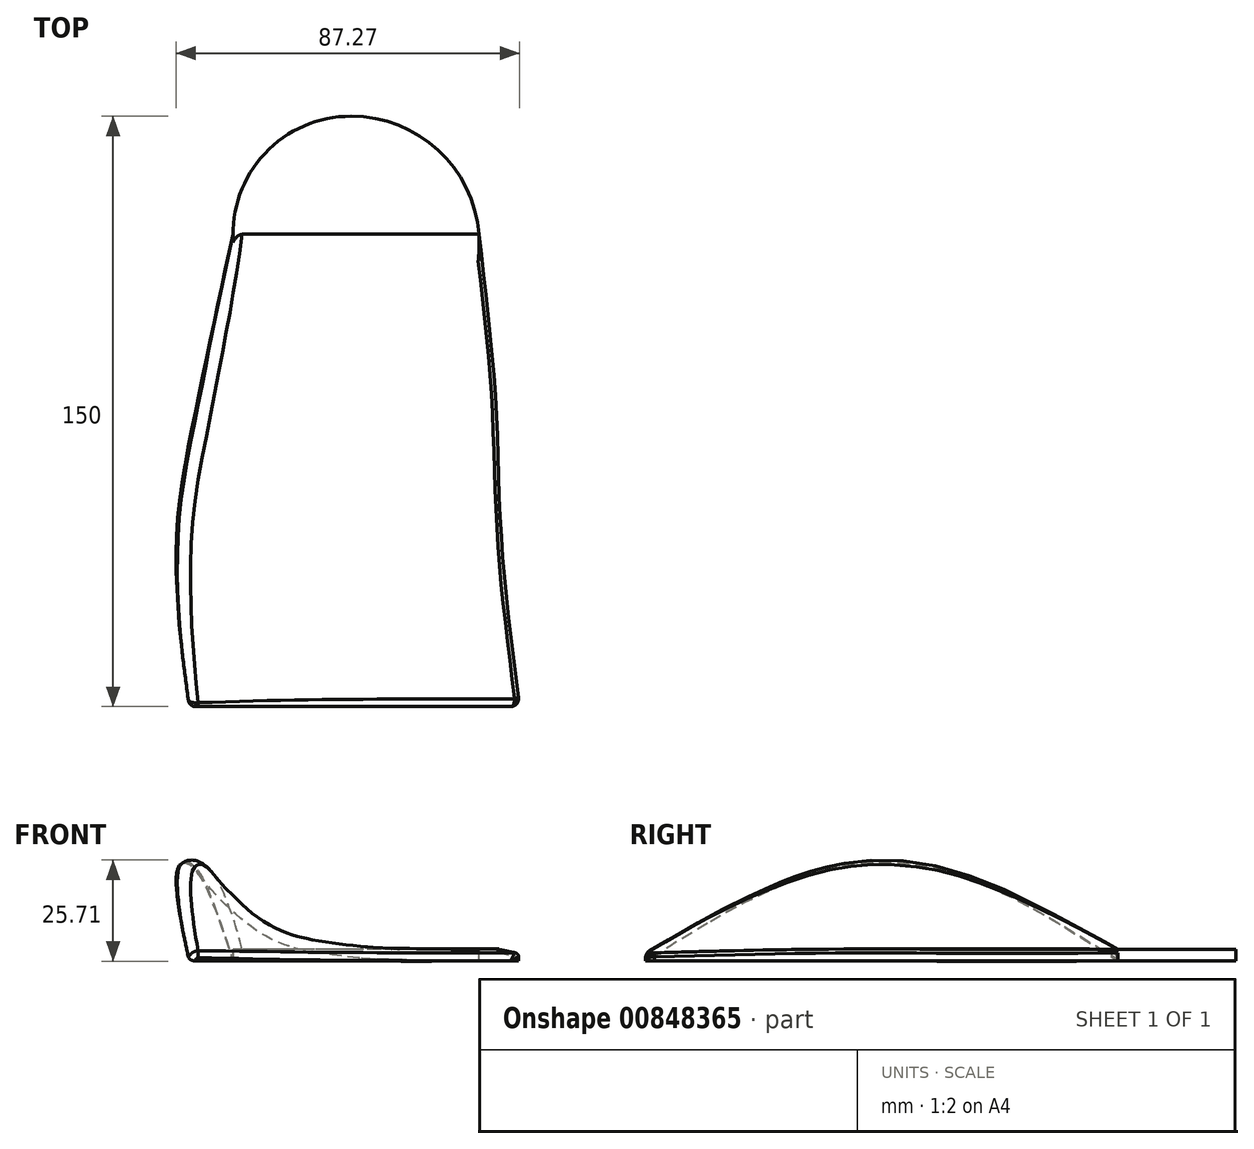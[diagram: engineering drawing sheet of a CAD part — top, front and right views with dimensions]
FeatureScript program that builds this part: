
annotation { "Feature Type Name" : "Feature", "Feature Type Description" : "" }
export const myFeature = defineFeature(function(context is Context, id is Id, definition is map)
    precondition{}
    {
        {
            var Q0;
            Q0=qCreatedBy(makeId("Top.planeOp"),FACE);
            var sketch = newSketch(context, id + "F0", { "sketchPlane" : qUnion([Q0])});
            skLineSegment(sketch, "E0", {"start": v(-30, 46.66) * mm, "end": v(0, 46.66) * mm});
            skLineSegment(sketch, "E1", {"start": v(0, 46.66) * mm, "end": v(32.5, 46.66) * mm});
            skLineSegment(sketch, "E2", {"start": v(0, 46.66) * mm, "end": v(0, 76.66) * mm});
            skArc(sketch, "E3", {"start": v(0, 76.66) * mm, "mid": v(-21.21, 67.87) * mm, "end": v(-30, 46.66) * mm});
            skArc(sketch, "E4", {"start": v(32.5, 46.66) * mm, "mid": v(22.14, 68.04) * mm, "end": v(0, 76.66) * mm});
            skLineSegment(sketch, "E5", {"start": v(0, 46.66) * mm, "end": v(0, 0) * mm});
            skLineSegment(sketch, "E6", {"start": v(0, 0) * mm, "end": v(-36, 0) * mm});
            skLineSegment(sketch, "E7", {"start": v(0, 0) * mm, "end": v(37, 0) * mm});
            skLineSegment(sketch, "E8", {"start": v(0, 0) * mm, "end": v(-0.14, -24.65) * mm});
            skLineSegment(sketch, "E9", {"start": v(-0.14, -24.65) * mm, "end": v(37.86, -24.65) * mm});
            skLineSegment(sketch, "E10", {"start": v(-0.14, -24.65) * mm, "end": v(-41.14, -24.65) * mm});
            skLineSegment(sketch, "E11", {"start": v(-0.14, -24.65) * mm, "end": v(-0.14, -73.34) * mm});
            skLineSegment(sketch, "E12", {"start": v(-0.14, -73.34) * mm, "end": v(42.86, -73.34) * mm});
            skLineSegment(sketch, "E13", {"start": v(-0.14, -73.34) * mm, "end": v(-41.14, -73.12) * mm});
            skFitSpline(sketch, "E14", {"points": [v(32.5, 46.66) * mm, v(37, 0) * mm, v(37.86, -24.65) * mm, v(42.86, -73.34) * mm], "startDerivative": vector(22.4, -132.76) * mm, "endDerivative": vector(27.8, -141.25) * mm});
            skSolve(sketch);
        }
        {
            var Q0;
            Q0=qCreatedBy(makeId("Front.planeOp"),FACE);
            var sketch = newSketch(context, id + "F1", { "sketchPlane" : qUnion([Q0])});
            skFitSpline(sketch, "E15.MirrorCS", {"points": [v(-37.41, 25.24) * mm, v(-31.18, 17.62) * mm, v(-24.67, 11.46) * mm, v(-17.5, 7.4) * mm, v(-8.82, 5.22) * mm, v(2.63, 3.7) * mm, v(13.1, 3) * mm, v(25.76, 3.04) * mm, v(37, 2.98) * mm], "startDerivative": vector(46.25, -63.9) * mm, "endDerivative": vector(92.16, -1.1) * mm});
            skFitSpline(sketch, "E16.0", {"points": [v(-39.84, 23.48) * mm, v(-38.84, 22.1) * mm, v(-37.24, 20.03) * mm, v(-35.28, 17.71) * mm, v(-34.14, 16.42) * mm, v(-33, 15.15) * mm, v(-31.55, 13.6) * mm, v(-29.74, 11.82) * mm, v(-27.86, 10.14) * mm, v(-25.86, 8.57) * mm, v(-23.76, 7.15) * mm, v(-21.56, 5.9) * mm, v(-19.64, 5) * mm, v(-18.06, 4.39) * mm, v(-16.47, 3.84) * mm, v(-14.45, 3.27) * mm, v(-11.97, 2.72) * mm, v(-9.83, 2.34) * mm, v(-8.07, 2.05) * mm, v(-6.27, 1.77) * mm, v(-3.96, 1.45) * mm, v(-1.18, 1.1) * mm, v(1.57, 0.78) * mm, v(4.22, 0.52) * mm, v(6.8, 0.3) * mm, v(9.4, 0.13) * mm, v(12.06, 0.02) * mm, v(14.87, -0.04) * mm, v(17.77, -0.04) * mm, v(20.7, -0.02) * mm, v(23.1, 0.01) * mm, v(24.97, 0.03) * mm, v(26.78, 0.04) * mm, v(28.96, 0.05) * mm, v(32.4, 0.03) * mm, v(35.05, 0) * mm, v(36.96, -0.02) * mm]});
            skLineSegment(sketch, "E17", {"start": v(-39.84, 23.48) * mm, "end": v(-37.41, 25.24) * mm});
            skLineSegment(sketch, "E18", {"start": v(37, 2.98) * mm, "end": v(36.96, -0.02) * mm});
            skSolve(sketch);
        }
        {
            var Q0;
            Q0=qCreatedBy(makeId("Front.planeOp"),FACE);
            cPlane(context, id + "F2", {"entities" : qUnion([Q0]), "cplaneType" : CPlaneType.OFFSET, "offset" : 24.6 * mm, "width" : 150 * mm, "height" : 150 * mm});
        }
        {
            var Q0;
            Q0=qCreatedBy(id+"F2.planeOp",FACE);
            var sketch = newSketch(context, id + "F3", { "sketchPlane" : qUnion([Q0])});
            skFitSpline(sketch, "E19.MirrorCS", {"points": [v(-41.5, 25.44) * mm, v(-35.26, 17.82) * mm, v(-28.75, 11.66) * mm, v(-21.59, 7.6) * mm, v(-12.9, 5.41) * mm, v(-0.98, 3.9) * mm, v(10.39, 3.27) * mm, v(21.43, 3.04) * mm, v(37.87, 3) * mm], "startDerivative": vector(46.25, -63.9) * mm, "endDerivative": vector(92.1, -0.52) * mm});
            skFitSpline(sketch, "E20.0", {"points": [v(-43.92, 23.68) * mm, v(-43.42, 22.99) * mm, v(-42.37, 21.59) * mm, v(-40.7, 19.5) * mm, v(-39.25, 17.78) * mm, v(-38.07, 16.45) * mm, v(-36.89, 15.14) * mm, v(-35.39, 13.56) * mm, v(-33.53, 11.74) * mm, v(-31.58, 10.04) * mm, v(-29.51, 8.46) * mm, v(-27.33, 7.04) * mm, v(-25.43, 6) * mm, v(-23.86, 5.27) * mm, v(-22.65, 4.78) * mm, v(-21.42, 4.33) * mm, v(-19.78, 3.81) * mm, v(-17.69, 3.27) * mm, v(-15.12, 2.75) * mm, v(-12.45, 2.3) * mm, v(-9.65, 1.87) * mm, v(-6.75, 1.49) * mm, v(-3.81, 1.15) * mm, v(-0.86, 0.87) * mm, v(2.04, 0.66) * mm, v(4.88, 0.5) * mm, v(7.64, 0.36) * mm, v(10.32, 0.26) * mm, v(12.9, 0.18) * mm, v(15.5, 0.12) * mm, v(18.24, 0.07) * mm, v(21.2, 0.04) * mm, v(24.49, 0.02) * mm, v(27.96, 0.01) * mm, v(31.47, 0.01) * mm, v(34.84, 0.01) * mm, v(36.9, 0) * mm, v(37.85, 0) * mm]});
            skLineSegment(sketch, "E21", {"start": v(-43.92, 23.68) * mm, "end": v(-41.5, 25.44) * mm});
            skLineSegment(sketch, "E22", {"start": v(37.85, 0) * mm, "end": v(37.87, 3) * mm});
            skSolve(sketch);
        }
        {
            var Q0;
            Q0=sQuery(id+"F0.wireOp",VERTEX,"E11.end");
            var Q1;
            Q1=qCreatedBy(id+"F2.planeOp",FACE);
            cPlane(context, id + "F4", {"entities" : qUnion([Q0, Q1]), "cplaneType" : CPlaneType.PLANE_POINT, "offset" : 25 * mm, "width" : 150 * mm, "height" : 150 * mm});
        }
        {
            var Q0;
            Q0=qCreatedBy(id+"F4.planeOp",FACE);
            var sketch = newSketch(context, id + "F5", { "sketchPlane" : qUnion([Q0])});
            skPoint(sketch, "E23.0", {"position": v(-41.14, 0) * mm});
            skPoint(sketch, "E24.0", {"position": v(42.86, 0) * mm});
            skLineSegment(sketch, "E25", {"start": v(-41.14, 2) * mm, "end": v(-41.14, 0) * mm});
            skLineSegment(sketch, "E26", {"start": v(42.86, 2) * mm, "end": v(42.86, 0) * mm});
            skLineSegment(sketch, "E27", {"start": v(-41.14, 0) * mm, "end": v(42.86, 0) * mm});
            skLineSegment(sketch, "E28", {"start": v(42.86, 2) * mm, "end": v(-41.14, 2) * mm});
            skSolve(sketch);
        }
        {
            var Q0;
            Q0=sQuery(id+"F0.wireOp",VERTEX,"E0.end");
            var Q1;
            Q1=qCreatedBy(makeId("Front.planeOp"),FACE);
            cPlane(context, id + "F6", {"entities" : qUnion([Q0, Q1]), "cplaneType" : CPlaneType.PLANE_POINT, "offset" : 25 * mm, "width" : 150 * mm, "height" : 150 * mm});
        }
        {
            var Q0;
            Q0=qCreatedBy(id+"F6.planeOp",FACE);
            var sketch = newSketch(context, id + "F7", { "sketchPlane" : qUnion([Q0])});
            skPoint(sketch, "E29.0", {"position": v(32.5, 0) * mm});
            skPoint(sketch, "E30.0", {"position": v(-30, 0) * mm});
            skLineSegment(sketch, "E31.bottom", {"start": v(32.5, 0) * mm, "end": v(-30, 0) * mm});
            skLineSegment(sketch, "E31.top", {"start": v(32.5, 3) * mm, "end": v(-30, 3) * mm});
            skLineSegment(sketch, "E31.left", {"start": v(32.5, 0) * mm, "end": v(32.5, 3) * mm});
            skLineSegment(sketch, "E31.right", {"start": v(-30, 0) * mm, "end": v(-30, 3) * mm});
            skSolve(sketch);
        }
        {
            var Q0;
            Q0=makeQuery(id+"F5.imprint","IMPRINT",FACE,{"disambiguationData":[TD([[makeQuery(id+"F5.imprint","IMPRINT",EDGE,{"derivedFrom":sQuery(id+"F5.wireOp",EDGE,"E25")}),1.0]])]});
            var Q1;
            Q1=makeQuery(id+"F3.imprint","IMPRINT",FACE,{"disambiguationData":[TD([[makeQuery(id+"F3.imprint","IMPRINT",EDGE,{"derivedFrom":sQuery(id+"F3.wireOp",EDGE,"E19.MirrorCS")}),-1.0]])]});
            var Q2;
            Q2=makeQuery(id+"F1.imprint","IMPRINT",FACE,{"disambiguationData":[TD([[makeQuery(id+"F1.imprint","IMPRINT",EDGE,{"derivedFrom":sQuery(id+"F1.wireOp",EDGE,"E15.MirrorCS")}),-1.0]])]});
            var Q3;
            Q3=makeQuery(id+"F7.imprint","IMPRINT",FACE,{"disambiguationData":[TD([[makeQuery(id+"F7.imprint","IMPRINT",EDGE,{"derivedFrom":sQuery(id+"F7.wireOp",EDGE,"E31.bottom")}),-1.0]])]});
            loft(context, id + "F8", {"sheetProfilesArray" : [{ "sheetProfileEntities" : qUnion([Q0]) }, { "sheetProfileEntities" : qUnion([Q1]) }, { "sheetProfileEntities" : qUnion([Q2]) }, { "sheetProfileEntities" : qUnion([Q3]) }]});
        }
        {
            var Q0;
            Q0=makeQuery(id+"F0.imprint","IMPRINT",FACE,{"disambiguationData":[TD([[makeQuery(id+"F0.imprint","IMPRINT",EDGE,{"derivedFrom":sQuery(id+"F0.wireOp",EDGE,"E0")}),1.0]])]});
            var Q1;
            Q1=makeQuery(id+"F0.imprint","IMPRINT",FACE,{"disambiguationData":[TD([[makeQuery(id+"F0.imprint","IMPRINT",EDGE,{"derivedFrom":sQuery(id+"F0.wireOp",EDGE,"E1")}),1.0]])]});
            extrude(context, id + "F9", {"entities" : qUnion([Q0, Q1]), "operationType" : NewBodyOperationType.ADD, "depth" : 3 * mm, "offsetDistance" : 25 * mm});
        }
        {
            var Q0;
            Q0=qCreatedBy(makeId("Top.planeOp"),FACE);
            cPlane(context, id + "F10", {"entities" : qUnion([Q0]), "cplaneType" : CPlaneType.OFFSET, "offset" : 3 * mm, "width" : 150 * mm, "height" : 150 * mm});
        }
        {
            var Q0;
            Q0=makeQuery(id+"F8.opLoft","SWEPT_EDGE",EDGE,{"disambiguationData":[OSD([sQuery(id+"F1.wireOp",EDGE,"E15.MirrorCS"),sQuery(id+"F1.wireOp",EDGE,"E18"),sQuery(id+"F3.wireOp",EDGE,"E19.MirrorCS"),sQuery(id+"F3.wireOp",EDGE,"E22"),sQuery(id+"F5.wireOp",EDGE,"E26"),sQuery(id+"F5.wireOp",EDGE,"E28"),sQuery(id+"F7.wireOp",EDGE,"E31.top"),sQuery(id+"F7.wireOp",EDGE,"E31.left")])]});
            fillet(context, id + "F11", {"entities" : qUnion([Q0]), "radius" : 1 * mm, "tangentPropagation" : true, "allowEdgeOverflow" : false});
        }
        {
            var Q0;
            Q0=makeQuery(id+"F8.opLoft","SWEPT_EDGE",EDGE,{"disambiguationData":[OSD([sQuery(id+"F1.wireOp",EDGE,"E15.MirrorCS"),sQuery(id+"F1.wireOp",EDGE,"E17"),sQuery(id+"F3.wireOp",EDGE,"E19.MirrorCS"),sQuery(id+"F3.wireOp",EDGE,"E21"),sQuery(id+"F5.wireOp",EDGE,"E25"),sQuery(id+"F5.wireOp",EDGE,"E28"),sQuery(id+"F7.wireOp",EDGE,"E31.top"),sQuery(id+"F7.wireOp",EDGE,"E31.right")])]});
            fillet(context, id + "F12", {"entities" : qUnion([Q0]), "radius" : 2.58 * mm, "tangentPropagation" : true, "allowEdgeOverflow" : false});
        }
        {
            var Q0;
            Q0=makeQuery(id+"F8.opLoft","MID_CAP_EDGE",EDGE,{"disambiguationData":[OSD([sQuery(id+"F5.wireOp",EDGE,"E25"),sQuery(id+"F5.wireOp",EDGE,"E26"),sQuery(id+"F5.wireOp",EDGE,"E28")])],"capPos":0.0});
            fillet(context, id + "F13", {"entities" : qUnion([Q0]), "radius" : 2 * mm, "tangentPropagation" : true, "allowEdgeOverflow" : false});
        }
    });
